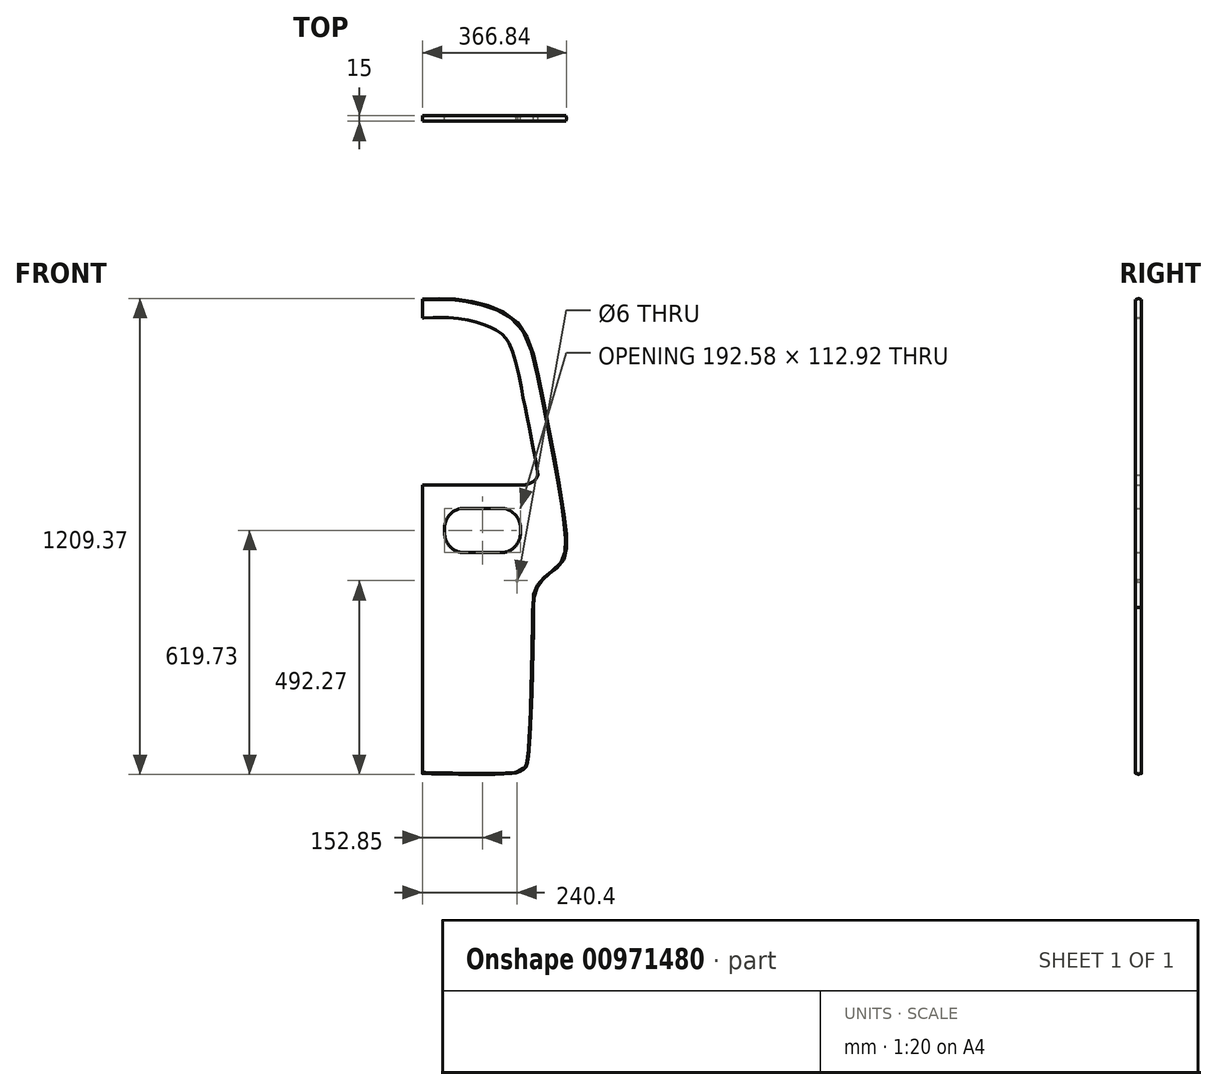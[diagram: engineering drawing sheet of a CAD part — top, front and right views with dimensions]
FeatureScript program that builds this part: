
annotation { "Feature Type Name" : "Feature", "Feature Type Description" : "" }
export const myFeature = defineFeature(function(context is Context, id is Id, definition is map)
    precondition{}
    {
        {
            var Q0;
            Q0=qCreatedBy(makeId("Front.planeOp"),FACE);
            var sketch = newSketch(context, id + "F0", { "sketchPlane" : qUnion([Q0])});
            skLineSegment(sketch, "E0", {"start": v(0, 0) * mm, "end": v(0, 1200) * mm});
            skLineSegment(sketch, "E1", {"start": v(280, 5.82) * mm, "end": v(280, 505.82) * mm, "construction": true});
            skPoint(sketch, "E2", {"position": v(320, 505.82) * mm});
            skPoint(sketch, "E3", {"position": v(300, 486.56) * mm});
            skPoint(sketch, "E4", {"position": v(280, 419.74) * mm});
            skPoint(sketch, "E5", {"position": v(285, 462.63) * mm});
            skPoint(sketch, "E6", {"position": v(350.37, 532.02) * mm});
            skPoint(sketch, "E7", {"position": v(363.2, 567.32) * mm});
            skPoint(sketch, "E8", {"position": v(360.8, 625.1) * mm});
            skPoint(sketch, "E9", {"position": v(339.76, 762.91) * mm});
            skPoint(sketch, "E10", {"position": v(301.84, 957.25) * mm});
            skPoint(sketch, "E11", {"position": v(254.23, 1123.01) * mm});
            skPoint(sketch, "E12", {"position": v(193.25, 1172.76) * mm});
            skPoint(sketch, "E13", {"position": v(125.03, 1193.96) * mm});
            skPoint(sketch, "E14", {"position": v(58.24, 1201.59) * mm});
            skPoint(sketch, "E15", {"position": v(0, 1200) * mm});
            skFitSpline(sketch, "E16", {"points": [v(0, 1200) * mm, v(58.24, 1201.59) * mm, v(125.03, 1193.96) * mm, v(193.25, 1172.76) * mm, v(254.23, 1123.01) * mm, v(301.84, 957.25) * mm, v(339.76, 762.91) * mm, v(360.8, 625.1) * mm, v(363.2, 567.32) * mm, v(350.37, 532.02) * mm, v(320, 505.82) * mm, v(300, 486.56) * mm, v(285, 462.63) * mm, v(280, 419.74) * mm], "startDerivative": vector(819.66, 46.4) * mm, "endDerivative": vector(4.36, -893.12) * mm});
            skPoint(sketch, "E17", {"position": v(264.2, 23.49) * mm});
            skPoint(sketch, "E18", {"position": v(257.11, 11.16) * mm});
            skPoint(sketch, "E19", {"position": v(245.64, 4.75) * mm});
            skPoint(sketch, "E20", {"position": v(229.45, 0) * mm});
            skFitSpline(sketch, "E21", {"points": [v(280, 419.74) * mm, v(264.2, 23.49) * mm, v(257.11, 11.16) * mm, v(245.64, 4.75) * mm, v(229.45, 0) * mm, v(0, 0) * mm], "startDerivative": vector(-22.66, -1251.8) * mm, "endDerivative": vector(-914.42, 18.8) * mm});
            skFitSpline(sketch, "E22.0", {"points": [v(2.26, 1160.06) * mm, v(6.53, 1160.3) * mm, v(14.95, 1160.78) * mm, v(27.3, 1161.37) * mm, v(37.43, 1161.67) * mm, v(45.48, 1161.76) * mm, v(50.5, 1161.74) * mm, v(54.5, 1161.67) * mm, v(57.51, 1161.6) * mm, v(60.53, 1161.5) * mm, v(64.6, 1161.32) * mm, v(69.7, 1161.03) * mm, v(77.98, 1160.42) * mm, v(88.45, 1159.36) * mm, v(101.14, 1157.64) * mm, v(111.74, 1155.82) * mm, v(120.2, 1154.14) * mm, v(128.6, 1152.3) * mm, v(138.97, 1149.72) * mm, v(149.12, 1146.73) * mm, v(157.1, 1144.08) * mm, v(163.01, 1141.96) * mm, v(167.87, 1140.08) * mm, v(171.7, 1138.5) * mm, v(174.09, 1137.5) * mm, v(175.98, 1136.66) * mm, v(177.87, 1135.82) * mm, v(180.19, 1134.76) * mm, v(182.88, 1133.47) * mm, v(186.37, 1131.73) * mm, v(190.52, 1129.5) * mm, v(195.18, 1126.73) * mm, v(199.54, 1123.82) * mm, v(203.6, 1120.74) * mm, v(207.43, 1117.46) * mm, v(211.04, 1113.91) * mm, v(213.91, 1110.67) * mm, v(216.14, 1107.86) * mm, v(217.78, 1105.63) * mm, v(219.12, 1103.67) * mm, v(220.18, 1102.02) * mm, v(221.23, 1100.32) * mm, v(222.57, 1098.04) * mm, v(224.72, 1094.08) * mm, v(227.4, 1088.57) * mm, v(230.59, 1081.13) * mm, v(233.7, 1072.93) * mm, v(236.7, 1064.05) * mm, v(239.6, 1054.56) * mm, v(243.34, 1041.16) * mm, v(247.74, 1023.22) * mm, v(251.87, 1004.08) * mm, v(255.07, 988.26) * mm, v(257.44, 976.2) * mm, v(259.41, 966.02) * mm, v(261, 957.83) * mm, v(262.18, 951.67) * mm, v(263.38, 945.5) * mm, v(264.58, 939.34) * mm, v(265.78, 933.2) * mm, v(267.38, 925.03) * mm, v(269.4, 914.86) * mm, v(272.6, 898.68) * mm, v(276.62, 878.62) * mm, v(281.38, 854.83) * mm, v(287.6, 823.5) * mm, v(292.84, 796.65) * mm, v(297.07, 774.05) * mm, v(299.13, 762.84) * mm, v(301.14, 751.72) * mm, v(303.08, 740.67) * mm, v(304.96, 729.74) * mm, v(307.38, 715.33) * mm, v(310.24, 697.71) * mm, v(313.37, 677.4) * mm, v(315.71, 661.35) * mm, v(317.4, 649.14) * mm, v(318.6, 640.31) * mm, v(319.69, 631.86) * mm, v(320.51, 625.14) * mm, v(321.13, 619.98) * mm, v(321.7, 614.98) * mm, v(322.35, 609.08) * mm, v(323, 602.5) * mm, v(323.49, 596.44) * mm, v(323.82, 590.87) * mm, v(324, 585.76) * mm, v(324.02, 581.1) * mm, v(323.9, 577.54) * mm, v(323.75, 574.88) * mm, v(323.61, 573.3) * mm, v(323.49, 572.05) * mm, v(323.35, 570.84) * mm, v(323.16, 569.4) * mm, v(322.9, 567.77) * mm, v(322.54, 565.77) * mm, v(322.01, 563.55) * mm, v(321.33, 561.37) * mm, v(320.74, 559.9) * mm, v(320.27, 558.92) * mm, v(319.92, 558.25) * mm, v(319.62, 557.76) * mm, v(319.38, 557.38) * mm, v(319.2, 557.11) * mm, v(319.04, 556.9) * mm, v(318.91, 556.73) * mm, v(318.82, 556.6) * mm, v(318.72, 556.47) * mm, v(318.56, 556.28) * mm, v(318.34, 556.02) * mm, v(318.03, 555.66) * mm, v(317.55, 555.13) * mm, v(316.83, 554.39) * mm, v(315.77, 553.37) * mm, v(314.13, 551.87) * mm, v(311.65, 549.78) * mm, v(308.69, 547.46) * mm, v(306.09, 545.48) * mm, v(304.03, 543.93) * mm, v(301.87, 542.31) * mm, v(300, 540.9) * mm, v(298.46, 539.73) * mm, v(297.28, 538.83) * mm, v(296.28, 538.05) * mm, v(295.47, 537.42) * mm, v(294.66, 536.78) * mm, v(293.65, 535.98) * mm, v(292.06, 534.68) * mm, v(290.12, 533.06) * mm, v(287.84, 531.1) * mm, v(284.88, 528.47) * mm, v(281.32, 525.15) * mm, v(277.96, 521.77) * mm, v(275.38, 519.05) * mm, v(273.5, 517) * mm, v(271.96, 515.29) * mm, v(270.76, 513.92) * mm, v(269.87, 512.88) * mm, v(269, 511.85) * mm, v(268.1, 510.78) * mm, v(267.2, 509.7) * mm, v(265.98, 508.2) * mm, v(264.44, 506.25) * mm, v(262.57, 503.78) * mm, v(260.69, 501.2) * mm, v(258.19, 497.55) * mm, v(255.1, 492.65) * mm, v(252.15, 487.24) * mm, v(250.23, 483.18) * mm, v(249.18, 480.78) * mm, v(248.42, 478.94) * mm, v(247.8, 477.38) * mm, v(247.33, 476.1) * mm, v(246.65, 474.2) * mm, v(245.7, 471.34) * mm, v(244.6, 467.53) * mm, v(243.66, 463.75) * mm, v(242.87, 459.98) * mm, v(241.97, 455) * mm, v(241.15, 448.86) * mm, v(240.52, 441.56) * mm, v(240.16, 434.3) * mm, v(240, 427) * mm, v(239.99, 422.05) * mm, v(240, 419.55) * mm]});
            skLineSegment(sketch, "E23", {"start": v(256.98, 730.8) * mm, "end": v(0, 730.8) * mm});
            skArc(sketch, "E24.filletArc", {"start": v(256.98, 730.8) * mm, "mid": v(287.76, 745.24) * mm, "end": v(296.3, 778.14) * mm});
            skLineSegment(sketch, "E25.0", {"start": v(256.98, 736.8) * mm, "end": v(0, 736.8) * mm});
            skArc(sketch, "E25.1", {"start": v(256.98, 736.8) * mm, "mid": v(283.14, 749.07) * mm, "end": v(290.4, 777.04) * mm});
            skFitSpline(sketch, "E25.2", {"points": [v(2.6, 1154.07) * mm, v(6.87, 1154.32) * mm, v(15.27, 1154.8) * mm, v(27.55, 1155.37) * mm, v(37.56, 1155.67) * mm, v(45.5, 1155.76) * mm, v(50.44, 1155.74) * mm, v(54.38, 1155.68) * mm, v(57.33, 1155.6) * mm, v(60.3, 1155.5) * mm, v(64.29, 1155.33) * mm, v(69.32, 1155.04) * mm, v(77.45, 1154.44) * mm, v(87.75, 1153.4) * mm, v(98.15, 1152) * mm, v(106.49, 1150.64) * mm, v(112.74, 1149.5) * mm, v(118.98, 1148.26) * mm, v(125.16, 1146.91) * mm, v(131.3, 1145.45) * mm, v(139.39, 1143.34) * mm, v(147.34, 1141) * mm, v(155.15, 1138.41) * mm, v(160.92, 1136.34) * mm, v(165.65, 1134.5) * mm, v(169.4, 1132.97) * mm, v(171.72, 1131.98) * mm, v(173.56, 1131.17) * mm, v(175.4, 1130.35) * mm, v(177.65, 1129.32) * mm, v(180.25, 1128.08) * mm, v(183.6, 1126.4) * mm, v(187.57, 1124.28) * mm, v(191.98, 1121.65) * mm, v(196.06, 1118.92) * mm, v(199.84, 1116.06) * mm, v(203.37, 1113.03) * mm, v(206.13, 1110.32) * mm, v(208.27, 1108) * mm, v(209.83, 1106.15) * mm, v(211.37, 1104.22) * mm, v(212.88, 1102.16) * mm, v(214.13, 1100.34) * mm, v(215.1, 1098.82) * mm, v(216.09, 1097.24) * mm, v(217.34, 1095.1) * mm, v(219.37, 1091.35) * mm, v(221.94, 1086.09) * mm, v(225.02, 1078.9) * mm, v(228.04, 1070.92) * mm, v(231, 1062.22) * mm, v(233.85, 1052.88) * mm, v(237.52, 1039.67) * mm, v(241.89, 1021.89) * mm, v(246, 1002.85) * mm, v(249.19, 987.09) * mm, v(251.55, 975.05) * mm, v(253.52, 964.88) * mm, v(255.1, 956.7) * mm, v(256.29, 950.53) * mm, v(257.49, 944.35) * mm, v(258.69, 938.18) * mm, v(259.9, 932.04) * mm, v(261.5, 923.87) * mm, v(263.5, 913.7) * mm, v(265.92, 901.55) * mm, v(268.33, 889.48) * mm, v(271.53, 873.48) * mm, v(275.5, 853.66) * mm, v(281.72, 822.35) * mm, v(286.95, 795.52) * mm, v(291.17, 772.95) * mm, v(293.23, 761.76) * mm, v(295.23, 750.66) * mm, v(297.17, 739.64) * mm, v(299.05, 728.73) * mm, v(301.46, 714.35) * mm, v(304.31, 696.78) * mm, v(307.44, 676.52) * mm, v(309.77, 660.5) * mm, v(311.47, 648.32) * mm, v(312.65, 639.53) * mm, v(313.73, 631.1) * mm, v(314.56, 624.42) * mm, v(315.17, 619.28) * mm, v(315.74, 614.31) * mm, v(316.39, 608.46) * mm, v(317.02, 601.97) * mm, v(317.5, 596.01) * mm, v(317.83, 590.57) * mm, v(318, 585.63) * mm, v(318.02, 581.16) * mm, v(317.91, 577.8) * mm, v(317.76, 575.32) * mm, v(317.64, 573.83) * mm, v(317.52, 572.69) * mm, v(317.4, 571.57) * mm, v(317.22, 570.25) * mm, v(317, 568.79) * mm, v(316.66, 567.01) * mm, v(316.21, 565.12) * mm, v(315.66, 563.35) * mm, v(315.23, 562.28) * mm, v(314.9, 561.61) * mm, v(314.68, 561.2) * mm, v(314.51, 560.9) * mm, v(314.38, 560.7) * mm, v(314.28, 560.55) * mm, v(314.2, 560.43) * mm, v(314.13, 560.34) * mm, v(314.08, 560.28) * mm, v(314.02, 560.2) * mm, v(313.93, 560.1) * mm, v(313.79, 559.92) * mm, v(313.56, 559.66) * mm, v(313.19, 559.26) * mm, v(312.6, 558.64) * mm, v(311.68, 557.75) * mm, v(310.2, 556.4) * mm, v(307.88, 554.45) * mm, v(305.02, 552.2) * mm, v(302.47, 550.26) * mm, v(300.43, 548.73) * mm, v(298.27, 547.11) * mm, v(296.38, 545.69) * mm, v(294.82, 544.5) * mm, v(293.62, 543.58) * mm, v(292.6, 542.79) * mm, v(291.76, 542.14) * mm, v(290.93, 541.48) * mm, v(289.9, 540.65) * mm, v(288.25, 539.32) * mm, v(286.24, 537.65) * mm, v(283.89, 535.62) * mm, v(280.83, 532.9) * mm, v(277.15, 529.46) * mm, v(273.66, 525.96) * mm, v(271, 523.15) * mm, v(269.04, 521.03) * mm, v(267.47, 519.26) * mm, v(266.23, 517.85) * mm, v(265.31, 516.79) * mm, v(264.41, 515.72) * mm, v(263.49, 514.62) * mm, v(262.56, 513.5) * mm, v(261.3, 511.94) * mm, v(259.7, 509.92) * mm, v(257.75, 507.36) * mm, v(255.79, 504.65) * mm, v(253.17, 500.84) * mm, v(249.92, 495.7) * mm, v(246.81, 489.98) * mm, v(244.77, 485.68) * mm, v(243.66, 483.14) * mm, v(242.85, 481.18) * mm, v(242.2, 479.52) * mm, v(241.7, 478.17) * mm, v(241.21, 476.82) * mm, v(240.63, 475.14) * mm, v(239.77, 472.44) * mm, v(238.8, 469.08) * mm, v(237.81, 465.09) * mm, v(236.98, 461.13) * mm, v(236.04, 455.92) * mm, v(235.18, 449.5) * mm, v(234.53, 441.96) * mm, v(234.16, 434.5) * mm, v(234, 427.05) * mm, v(233.99, 422.05) * mm, v(234, 419.52) * mm]});
            skPoint(sketch, "E26", {"position": v(237.73, 957) * mm});
            skLineSegment(sketch, "E27", {"start": v(253.15, 966.77) * mm, "end": v(257.94, 942.04) * mm, "construction": true});
            skLineSegment(sketch, "E28", {"start": v(2.26, 1160.06) * mm, "end": v(0, 1159.94) * mm});
            skLineSegment(sketch, "E29", {"start": v(2.6, 1154.07) * mm, "end": v(0, 1153.96) * mm});
            skPoint(sketch, "E30", {"position": v(152.65, 614.74) * mm});
            skLineSegment(sketch, "E31.bottom", {"start": v(106.36, 671.2) * mm, "end": v(198.94, 671.2) * mm});
            skLineSegment(sketch, "E31.top", {"start": v(106.36, 558.28) * mm, "end": v(198.94, 558.28) * mm});
            skLineSegment(sketch, "E31.left", {"start": v(56.36, 621.2) * mm, "end": v(56.36, 608.28) * mm});
            skLineSegment(sketch, "E31.right", {"start": v(248.94, 621.2) * mm, "end": v(248.94, 608.28) * mm});
            skPoint(sketch, "E32.visualSharp", {"position": v(56.36, 671.2) * mm});
            skArc(sketch, "E32.filletArc", {"start": v(106.36, 671.2) * mm, "mid": v(71, 656.55) * mm, "end": v(56.36, 621.2) * mm});
            skPoint(sketch, "E33.visualSharp", {"position": v(56.36, 558.28) * mm});
            skArc(sketch, "E33.filletArc", {"start": v(56.36, 608.28) * mm, "mid": v(71, 572.92) * mm, "end": v(106.36, 558.28) * mm});
            skPoint(sketch, "E34.visualSharp", {"position": v(248.94, 558.28) * mm});
            skArc(sketch, "E34.filletArc", {"start": v(198.94, 558.28) * mm, "mid": v(234.3, 572.92) * mm, "end": v(248.94, 608.28) * mm});
            skPoint(sketch, "E35.visualSharp", {"position": v(248.94, 671.2) * mm});
            skArc(sketch, "E35.filletArc", {"start": v(248.94, 621.2) * mm, "mid": v(234.3, 656.55) * mm, "end": v(198.94, 671.2) * mm});
            skSolve(sketch);
        }
        {
            var Q0;
            {var subQ1=sQuery(id+"F0.wireOp",EDGE,"E16");Q0=makeQuery(id+"F0.imprint","IMPRINT",FACE,{"disambiguationData":[TD([[makeQuery(id+"F0.imprint","IMPRINT",EDGE,{"derivedFrom":subQ1}),-1.0]])]});}
            var Q1;
            {var subQ0=sQuery(id+"F0.wireOp",EDGE,"E25.0");Q1=makeQuery(id+"F0.imprint","IMPRINT",FACE,{"disambiguationData":[TD([[makeQuery(id+"F0.imprint","IMPRINT",EDGE,{"derivedFrom":subQ0}),-1.0]])]});}
            extrude(context, id + "F1", {"entities" : qUnion([Q0, Q1]), "depth" : 15 * mm, "offsetDistance" : 25 * mm});
        }
        {
            var Q0;
            Q0=sQuery(id+"F0.wireOp",VERTEX,"E26");
            var Q1;
            Q1=makeQuery(id+"F1.opExtrude","SWEPT_BODY",BODY,{"disambiguationData":[OSD([sQuery(id+"F0.wireOp",EDGE,"E0"),sQuery(id+"F0.wireOp",EDGE,"E25.0"),sQuery(id+"F0.wireOp",EDGE,"E25.1"),sQuery(id+"F0.wireOp",EDGE,"E25.2"),sQuery(id+"F0.wireOp",EDGE,"E29")])]});
            hole(context, id + "F2", {"style" : HoleStyle.SIMPLE, "endStyle" : HoleEndStyle.THROUGH, "oppositeDirection" : true, "holeDiameter" : 20 * mm, "majorDiameter" : 5 * mm, "isTappedThrough" : true, "tappedDepth" : 12 * mm, "tapClearance" : 3, "locations" : qUnion([Q0]), "scope" : qUnion([Q1])});
        }
        {
            var Q0;
            Q0=makeQuery(id+"F1.opExtrude","CAP_FACE",FACE,{"disambiguationData":[OSD([sQuery(id+"F0.wireOp",EDGE,"E0"),sQuery(id+"F0.wireOp",EDGE,"E16"),sQuery(id+"F0.wireOp",EDGE,"E21"),sQuery(id+"F0.wireOp",EDGE,"E22.0"),sQuery(id+"F0.wireOp",EDGE,"E23"),sQuery(id+"F0.wireOp",EDGE,"E24.filletArc"),sQuery(id+"F0.wireOp",EDGE,"E28"),sQuery(id+"F0.wireOp",EDGE,"E31.bottom"),sQuery(id+"F0.wireOp",EDGE,"E31.top"),sQuery(id+"F0.wireOp",EDGE,"E31.left"),sQuery(id+"F0.wireOp",EDGE,"E31.right"),sQuery(id+"F0.wireOp",EDGE,"E32.filletArc"),sQuery(id+"F0.wireOp",EDGE,"E33.filletArc"),sQuery(id+"F0.wireOp",EDGE,"E34.filletArc"),sQuery(id+"F0.wireOp",EDGE,"E35.filletArc")])],"isStart":true});
            var sketch = newSketch(context, id + "F3", { "sketchPlane" : qUnion([Q0])});
            skPoint(sketch, "E36", {"position": v(-240.2, 487.28) * mm});
            skSolve(sketch);
        }
        {
            var Q0;
            Q0=sQuery(id+"F3.wireOp",VERTEX,"E36");
            var Q1;
            Q1=makeQuery(id+"F1.opExtrude","SWEPT_BODY",BODY,{"disambiguationData":[OSD([sQuery(id+"F0.wireOp",EDGE,"E0"),sQuery(id+"F0.wireOp",EDGE,"E16"),sQuery(id+"F0.wireOp",EDGE,"E21"),sQuery(id+"F0.wireOp",EDGE,"E22.0"),sQuery(id+"F0.wireOp",EDGE,"E23"),sQuery(id+"F0.wireOp",EDGE,"E24.filletArc"),sQuery(id+"F0.wireOp",EDGE,"E28"),sQuery(id+"F0.wireOp",EDGE,"E31.bottom"),sQuery(id+"F0.wireOp",EDGE,"E31.top"),sQuery(id+"F0.wireOp",EDGE,"E31.left"),sQuery(id+"F0.wireOp",EDGE,"E31.right"),sQuery(id+"F0.wireOp",EDGE,"E32.filletArc"),sQuery(id+"F0.wireOp",EDGE,"E33.filletArc"),sQuery(id+"F0.wireOp",EDGE,"E34.filletArc"),sQuery(id+"F0.wireOp",EDGE,"E35.filletArc")])]});
            hole(context, id + "F4", {"style" : HoleStyle.SIMPLE, "endStyle" : HoleEndStyle.BLIND, "holeDiameter" : 6 * mm, "majorDiameter" : 5 * mm, "holeDepth" : 10 * mm, "isTappedThrough" : true, "tappedDepth" : 12 * mm, "tapClearance" : 3, "locations" : qUnion([Q0]), "scope" : qUnion([Q1])});
        }
        {
            var Q0;
            {var subQ0=sQuery(id+"F0.wireOp",EDGE,"E0");Q0=makeQuery(id+"F1.opExtrude","SWEPT_FACE",FACE,{"disambiguationData":[OSD([subQ0]),TDD([makeQuery(id+"F0.imprint","IMPRINT",EDGE,{"disambiguationData":[TD([[makeQuery(id+"F0.imprint","INTERSECT",VERTEX,{"derivedFrom":[subQ0,sQuery(id+"F0.wireOp",EDGE,"E28")]}),-1.0]])],"derivedFrom":subQ0})])]});}
            var sketch = newSketch(context, id + "F5", { "sketchPlane" : qUnion([Q0])});
            skLineSegment(sketch, "E37.bottom", {"start": v(15, 1200) * mm, "end": v(0, 1200) * mm});
            skLineSegment(sketch, "E37.left", {"start": v(15, 1200) * mm, "end": v(15, 1200.32) * mm});
            skLineSegment(sketch, "E37.right", {"start": v(0, 1200) * mm, "end": v(0, 1200.32) * mm});
            skPoint(sketch, "E38.startSnap0", {"position": v(7.5, 1200.32) * mm});
            skFitSpline(sketch, "E39", {"points": [v(15, 1200.32) * mm, v(11.64, 1200.71) * mm, v(7.36, 1202.64) * mm, v(3.15, 1200.65) * mm, v(0, 1200.32) * mm], "startDerivative": vector(-13.78, 1.9) * mm, "endDerivative": vector(-13.12, -1.6) * mm});
            skSolve(sketch);
        }
        {
            var Q0;
            Q0=makeQuery(id+"F5.imprint","IMPRINT",FACE,{"disambiguationData":[TD([[makeQuery(id+"F5.imprint","IMPRINT",EDGE,{"derivedFrom":sQuery(id+"F5.wireOp",EDGE,"E37.bottom")}),-1.0]])]});
            var Q1;
            Q1=makeQuery(id+"F1.opExtrude","CAP_EDGE",EDGE,{"disambiguationData":[OSD([sQuery(id+"F0.wireOp",EDGE,"E16")])],"isStart":false});
            var Q2;
            Q2=makeQuery(id+"F1.opExtrude","CAP_EDGE",EDGE,{"disambiguationData":[OSD([sQuery(id+"F0.wireOp",EDGE,"E21")])],"isStart":false});
            sweep(context, id + "F6", {"operationType" : NewBodyOperationType.ADD, "profiles" : qUnion([Q0]), "path" : qUnion([Q1, Q2])});
        }
    });
